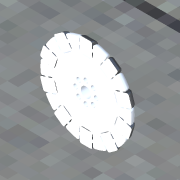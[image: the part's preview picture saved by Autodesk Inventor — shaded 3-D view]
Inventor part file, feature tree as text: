
AUTODESK INVENTOR PART (.ipt)
format: ipt  version: 2012 (Build 160160000, 160)  size: 867,840 bytes
history: native  units: in
note: dims shown in document units (in); Inventor stores cm internally (conversion verified against a paired STEP export)
features: sketch x8, extrude x4, fillet x4, pattern_circular x3, split x2, hole x1, revolve x1
ambient origin geometry x8: Origin, YZ Plane, XZ Plane, XY Plane, X Axis, Y Axis, Z Axis, Center Point
bodies: Solid1 (feature_tree)
feature tree (23):
  extrude  "Extrusion1"  Depth=0.4in TaperAngle=0.0deg
  fillet  "Fillet1"  Radius=0.175in
  extrude  "Extrusion2"  Depth=0.5in TaperAngle=0.0deg
  hole  "Hole1"  [1 undecoded]
  pattern_circular  "Circular Pattern1"  [2 undecoded]
  extrude  "Extrusion3"  Depth=2.8in
  fillet  "Fillet2"  Radius=0.125in
  extrude  "Extrusion4"  Depth=0.05in
  fillet  "Fillet3"  Radius=3.937in
  split  "Split1"
  fillet  "Fillet4"  Radius=1.4in
  pattern_circular  "Circular Pattern2"  [2 undecoded]
  split  "Split2"
  revolve  "Revolution1"  [1 undecoded]
  pattern_circular  "Circular Pattern3"  Angle=180.0deg  [1 undecoded]
  sketch  "Sketch1"  dims[d0=2.8in d1=0.4in d2=0.0in d3=0.175in]
  sketch  "Sketch2"  dims[d4=0.175in d8=0.5in d9=0.0in]
  sketch  "Sketch3"  dims[d11=0.137in d12=0.75in d13=0.375in d14=0.25in d15=0.5635in d16=1.0in d17=0.8108in d18=3.1496in d19=360.0deg]
  sketch  "Sketch4"  dims[d21=1.75in]
  sketch  "Sketch5"  dims[d22=0.05in d23=0.0in]
  sketch  "Sketch6"  dims[d24=0.05in]
  sketch  "Sketch7"  dims[d25=1.75in]
  sketch  "Sketch8"  dims[d26=0.05in d27=0.0in d28=0.05in d31=2.8in d32=0.125in d33=0.05in d34=3.937in d35=360.0deg d37=1.4in d38=1.4in d39=0.05in d40=180.0deg d41=3.937in d42=360.0deg]
note: 7 required parameter values undecoded (feature->parameter linkage not recoverable at this tier; creation-order binding heuristic only, values carry confidence <= 0.55)